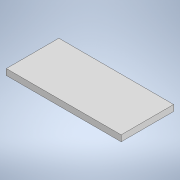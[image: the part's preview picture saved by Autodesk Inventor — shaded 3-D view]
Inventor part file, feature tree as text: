
AUTODESK INVENTOR PART (.ipt)
format: ipt  version: 2020 (Build 240168000, 168)  size: 90,112 bytes
history: native  units: in
note: dims shown in document units (in); Inventor stores cm internally (conversion verified against a paired STEP export)
features: sketch x2, extrude x1
ambient origin geometry x8: Origin, YZ Plane, XZ Plane, XY Plane, X Axis, Y Axis, Z Axis, Center Point
bodies: Solid1 (feature_tree)
feature tree (3):
  sketch  "3D Sketch1"
  extrude  "Extrusion1"  Depth=2.7in
  sketch  "Sketch1"  dims[d0=5.9in d1=2.7in d2=0.31in d3=0.0in]
